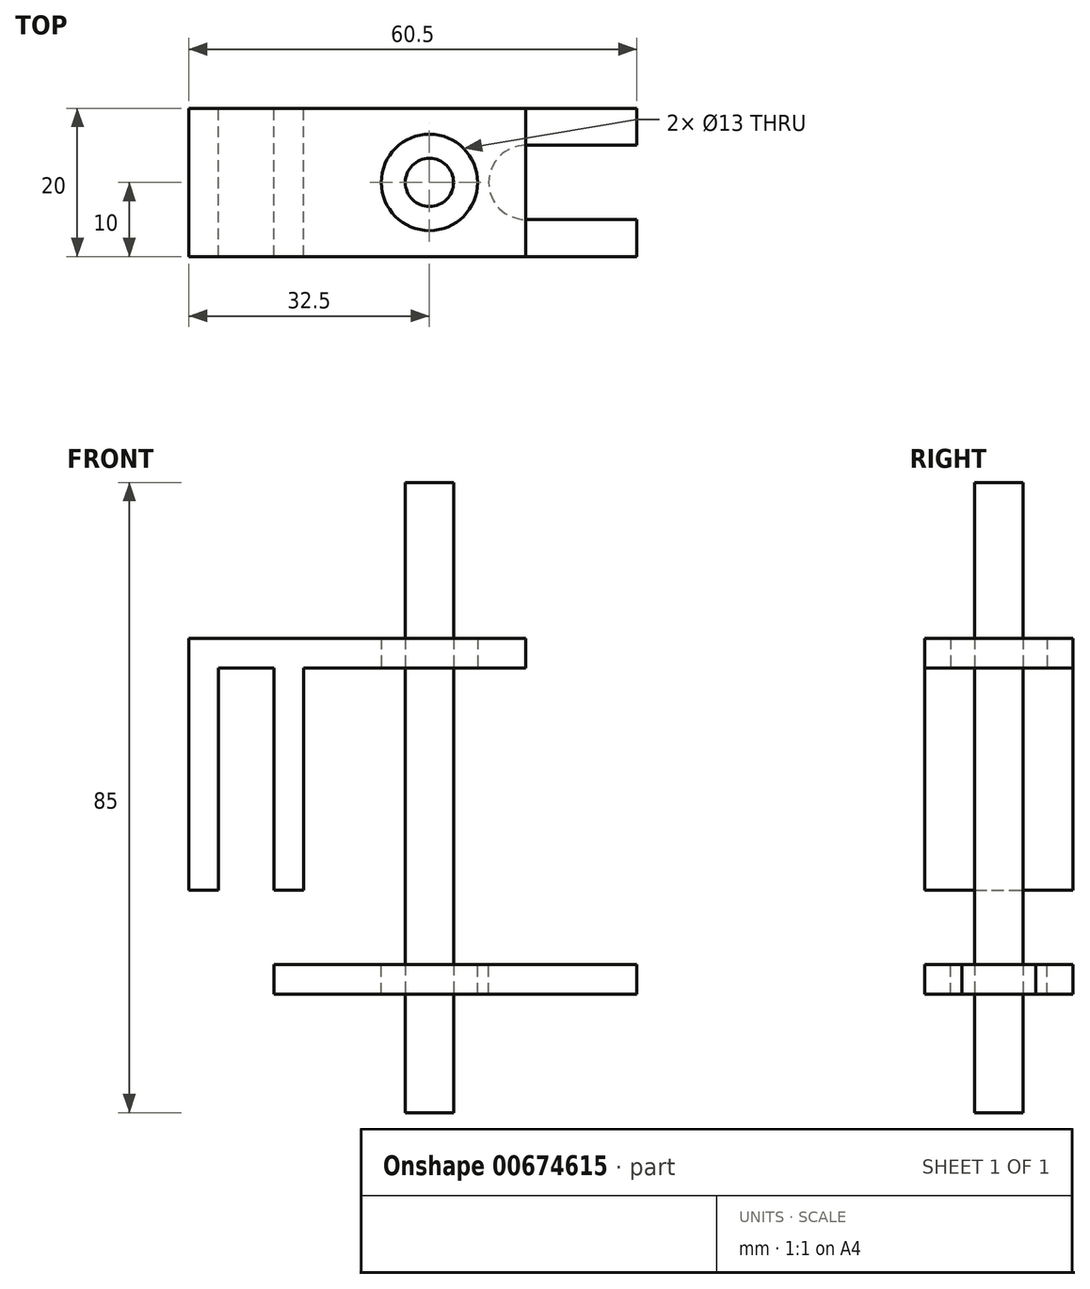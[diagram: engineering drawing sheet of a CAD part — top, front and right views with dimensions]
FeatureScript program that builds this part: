
annotation { "Feature Type Name" : "Feature", "Feature Type Description" : "" }
export const myFeature = defineFeature(function(context is Context, id is Id, definition is map)
    precondition{}
    {
        {
            var Q0;
            Q0=qCreatedBy(makeId("Front.planeOp"),FACE);
            var sketch = newSketch(context, id + "F0", { "sketchPlane" : qUnion([Q0])});
            skLineSegment(sketch, "E0", {"start": v(0, 0) * mm, "end": v(0, -30) * mm});
            skLineSegment(sketch, "E1", {"start": v(0, -30) * mm, "end": v(4, -30) * mm});
            skLineSegment(sketch, "E2", {"start": v(4, -30) * mm, "end": v(4, 0) * mm});
            skLineSegment(sketch, "E3", {"start": v(4, 0) * mm, "end": v(0, 0) * mm});
            skLineSegment(sketch, "E4", {"start": v(0, 0) * mm, "end": v(-7.5, 0) * mm});
            skLineSegment(sketch, "E5", {"start": v(-7.5, 0) * mm, "end": v(-7.5, -30) * mm});
            skLineSegment(sketch, "E6", {"start": v(-7.5, -30) * mm, "end": v(-11.5, -30) * mm});
            skLineSegment(sketch, "E7", {"start": v(-11.5, -30) * mm, "end": v(-11.5, 0) * mm});
            skLineSegment(sketch, "E8", {"start": v(-11.5, 0) * mm, "end": v(-7.5, 0) * mm});
            skLineSegment(sketch, "E9", {"start": v(-11.5, 0) * mm, "end": v(-11.5, 4) * mm});
            skLineSegment(sketch, "E10", {"start": v(-11.5, 4) * mm, "end": v(34, 4) * mm});
            skLineSegment(sketch, "E11", {"start": v(34, 4) * mm, "end": v(34, 0) * mm});
            skLineSegment(sketch, "E12", {"start": v(34, 0) * mm, "end": v(-7.5, 0) * mm});
            skSolve(sketch);
        }
        {
            var Q0;
            Q0 = qSketchRegion(id + "F0", true);
            extrude(context, id + "F1", {"entities" : qUnion([Q0]), "depth" : 10 * mm, "offsetDistance" : 25 * mm, "hasSecondDirection" : true, "secondDirectionOppositeDirection" : true, "secondDirectionDepth" : 10 * mm});
        }
        {
            var Q0;
            Q0=qCreatedBy(makeId("Top.planeOp"),FACE);
            var sketch = newSketch(context, id + "F2", { "sketchPlane" : qUnion([Q0])});
            skCircle(sketch, "E13", {"center": v(21, 0) * mm, "radius": 3.25 * mm, "construction": true});
            skCircle(sketch, "E14", {"center": v(21, 0) * mm, "radius": 6.5 * mm});
            skSolve(sketch);
        }
        {
            var Q0;
            Q0=makeQuery(id+"F2.imprint","IMPRINT",FACE,{"disambiguationData":[TD([[makeQuery(id+"F2.imprint","IMPRINT",EDGE,{"derivedFrom":sQuery(id+"F2.wireOp",EDGE,"E14")}),1.0]])]});
            extrude(context, id + "F3", {"entities" : qUnion([Q0]), "operationType" : NewBodyOperationType.REMOVE, "depth" : 11.1 * mm, "offsetDistance" : 25 * mm});
        }
        {
            var Q0;
            Q0=qCreatedBy(makeId("Top.planeOp"),FACE);
            var sketch = newSketch(context, id + "F4", { "sketchPlane" : qUnion([Q0])});
            skCircle(sketch, "E15.0", {"center": v(21, 0) * mm, "radius": 3.25 * mm});
            skSolve(sketch);
        }
        {
            var Q0;
            Q0 = qSketchRegion(id + "F4", true);
            extrude(context, id + "F5", {"entities" : qUnion([Q0]), "depth" : 25 * mm, "offsetDistance" : 25 * mm, "hasSecondDirection" : true, "secondDirectionOppositeDirection" : true, "secondDirectionDepth" : 60 * mm});
        }
        {
            var Q0;
            Q0=qCreatedBy(makeId("Top.planeOp"),FACE);
            cPlane(context, id + "F6", {"entities" : qUnion([Q0]), "cplaneType" : CPlaneType.OFFSET, "offset" : 40 * mm, "oppositeDirection" : true, "width" : 150 * mm, "height" : 150 * mm});
        }
        {
            var Q0;
            Q0=qCreatedBy(id+"F6.planeOp",FACE);
            var sketch = newSketch(context, id + "F7", { "sketchPlane" : qUnion([Q0])});
            skLineSegment(sketch, "E16.0.0", {"start": v(15, 10) * mm, "end": v(34, 10) * mm});
            skLineSegment(sketch, "E16.0.2", {"start": v(34, -10) * mm, "end": v(15, -10) * mm});
            skLineSegment(sketch, "E17.bottom", {"start": v(15, -10) * mm, "end": v(49, -10) * mm});
            skLineSegment(sketch, "E17.top", {"start": v(15, 10) * mm, "end": v(49, 10) * mm});
            skLineSegment(sketch, "E17.right", {"start": v(49, -10) * mm, "end": v(49, -5) * mm});
            skPoint(sketch, "E16.0.3.start.orphan", {"position": v(4, -10) * mm});
            skPoint(sketch, "E18.orphan", {"position": v(4, 10) * mm});
            skArc(sketch, "E19", {"start": v(34, 5) * mm, "mid": v(29, 0) * mm, "end": v(34, -5) * mm});
            skLineSegment(sketch, "E20", {"start": v(34, -10) * mm, "end": v(34, -5) * mm, "construction": true});
            skLineSegment(sketch, "E21", {"start": v(34, -5) * mm, "end": v(49, -5) * mm});
            skLineSegment(sketch, "E22.MirrorCS", {"start": v(34, 5) * mm, "end": v(49, 5) * mm});
            skLineSegment(sketch, "E23.trimOffspring", {"start": v(49, 5) * mm, "end": v(49, 10) * mm});
            skLineSegment(sketch, "E24.trimOffspring", {"start": v(34, 5) * mm, "end": v(34, 10) * mm, "construction": true});
            skLineSegment(sketch, "E25.0", {"start": v(0, -10) * mm, "end": v(0, 10) * mm});
            skLineSegment(sketch, "E26", {"start": v(0, -10) * mm, "end": v(15, -10) * mm});
            skLineSegment(sketch, "E27", {"start": v(0, 10) * mm, "end": v(15, 10) * mm});
            skCircle(sketch, "E28.0", {"center": v(21, 0) * mm, "radius": 6.5 * mm});
            skPoint(sketch, "E29", {"position": v(29, 0) * mm});
            skSolve(sketch);
        }
        {
            var Q0;
            Q0 = qSketchRegion(id + "F7", true);
            extrude(context, id + "F8", {"entities" : qUnion([Q0]), "oppositeDirection" : true, "depth" : 4 * mm, "offsetDistance" : 25 * mm});
        }
    });
